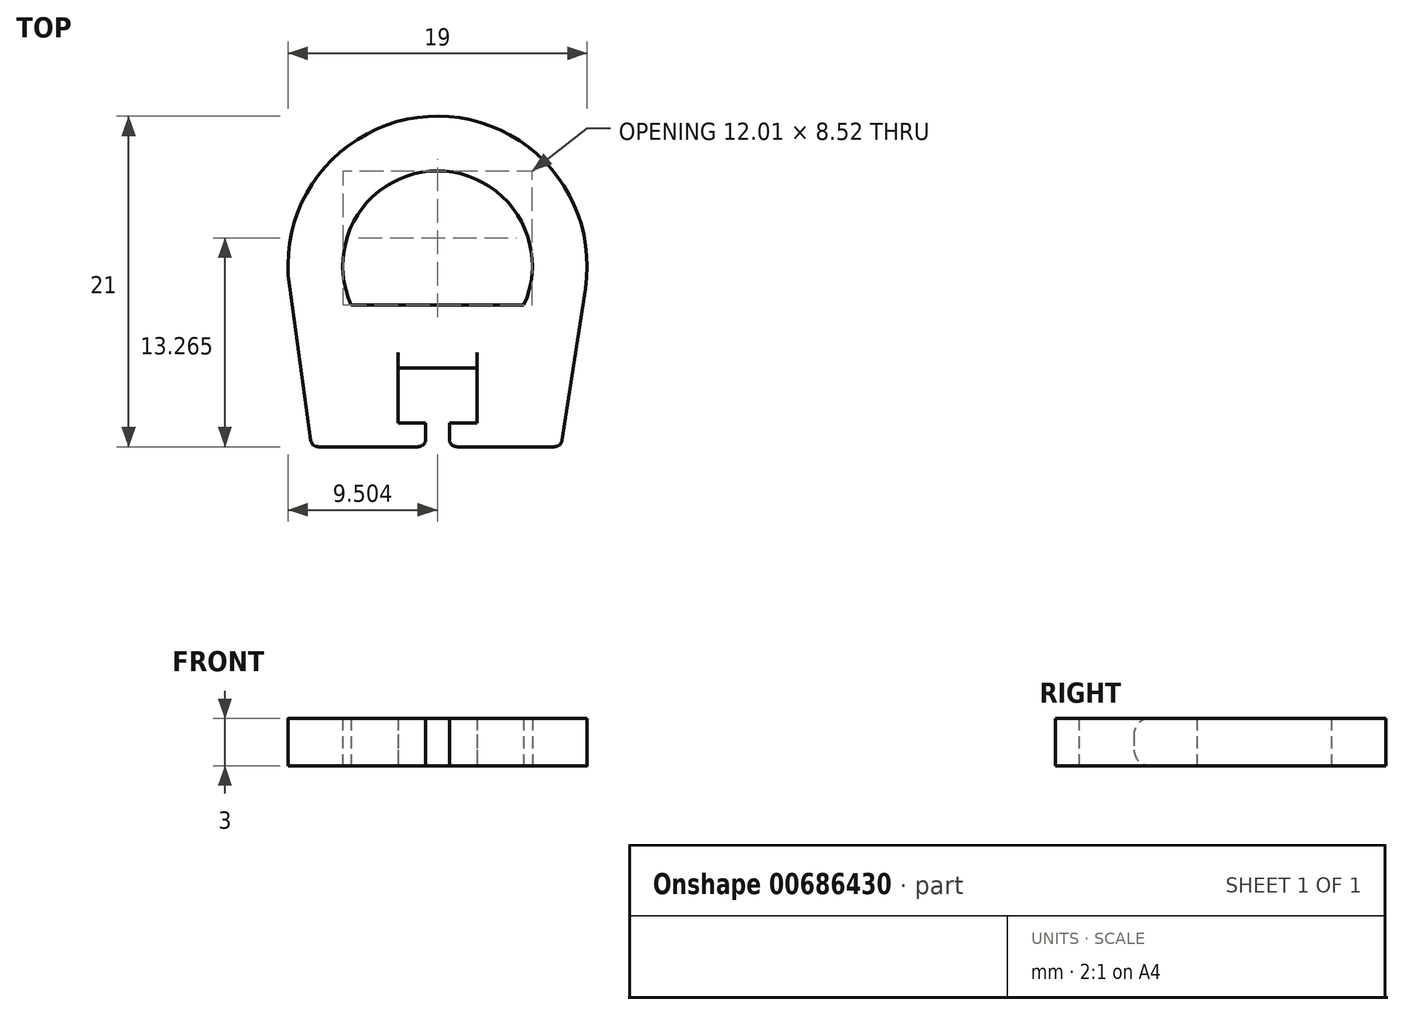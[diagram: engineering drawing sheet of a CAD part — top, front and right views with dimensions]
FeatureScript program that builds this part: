
annotation { "Feature Type Name" : "Feature", "Feature Type Description" : "" }
export const myFeature = defineFeature(function(context is Context, id is Id, definition is map)
    precondition{}
    {
        {
            var Q0;
            Q0=qCreatedBy(makeId("Top.planeOp"),FACE);
            var sketch = newSketch(context, id + "F0", { "sketchPlane" : qUnion([Q0])});
            skLineSegment(sketch, "E0.bottom", {"start": v(-28.7, 14.07) * mm, "end": v(-23.7, 14.07) * mm});
            skLineSegment(sketch, "E0.left", {"start": v(-28.7, 14.07) * mm, "end": v(-28.7, 10.57) * mm});
            skLineSegment(sketch, "E0.right", {"start": v(-23.7, 14.07) * mm, "end": v(-23.7, 10.57) * mm});
            skArc(sketch, "E1", {"start": v(-16.82, 19.13) * mm, "mid": v(-26.13, 30.07) * mm, "end": v(-35.62, 19.27) * mm});
            skPoint(sketch, "E1.centerSnap0", {"position": v(-26.2, 14.07) * mm});
            skLineSegment(sketch, "E2.0", {"start": v(-29.8, 9.07) * mm, "end": v(-26.96, 9.07) * mm});
            skLineSegment(sketch, "E3.0", {"start": v(-28.7, 10.57) * mm, "end": v(-26.96, 10.57) * mm});
            skLineSegment(sketch, "E4.0", {"start": v(-25.46, 10.57) * mm, "end": v(-25.46, 9.57) * mm});
            skLineSegment(sketch, "E5.0", {"start": v(-26.96, 10.57) * mm, "end": v(-26.96, 9.57) * mm});
            skPoint(sketch, "E6.end.orphan", {"position": v(-26.2, 9.07) * mm});
            skPoint(sketch, "E6.start.orphan", {"position": v(-26.2, 10.57) * mm});
            skLineSegment(sketch, "E7.trimOffspring", {"start": v(-25.46, 9.07) * mm, "end": v(-22.62, 9.07) * mm});
            skLineSegment(sketch, "E8.trimOffspring", {"start": v(-25.46, 9.07) * mm, "end": v(-23.7, 9.07) * mm});
            skLineSegment(sketch, "E9.trimOffspring", {"start": v(-25.46, 10.57) * mm, "end": v(-23.7, 10.57) * mm});
            skLineSegment(sketch, "E10", {"start": v(-33.77, 9.07) * mm, "end": v(-27.46, 9.07) * mm});
            skLineSegment(sketch, "E11.trimOffspring", {"start": v(-24.96, 9.07) * mm, "end": v(-18.8, 9.07) * mm});
            skLineSegment(sketch, "E12", {"start": v(-18.3, 9.5) * mm, "end": v(-16.82, 19.13) * mm});
            skLineSegment(sketch, "E13", {"start": v(-34.27, 9.5) * mm, "end": v(-35.62, 19.27) * mm});
            skLineSegment(sketch, "E14.0", {"start": v(-31.68, 18.07) * mm, "end": v(-20.73, 18.07) * mm});
            skArc(sketch, "E15.trimOffspring", {"start": v(-20.73, 18.07) * mm, "mid": v(-26.2, 26.6) * mm, "end": v(-31.68, 18.07) * mm});
            skPoint(sketch, "E16.visualSharp", {"position": v(-25.46, 9.07) * mm});
            skArc(sketch, "E16.filletArc", {"start": v(-25.46, 9.57) * mm, "mid": v(-25.31, 9.22) * mm, "end": v(-24.96, 9.07) * mm});
            skPoint(sketch, "E17.visualSharp", {"position": v(-26.96, 9.07) * mm});
            skArc(sketch, "E17.filletArc", {"start": v(-27.46, 9.07) * mm, "mid": v(-27.1, 9.22) * mm, "end": v(-26.96, 9.57) * mm});
            skPoint(sketch, "E18.visualSharp", {"position": v(-18.36, 9.07) * mm});
            skArc(sketch, "E18.filletArc", {"start": v(-18.8, 9.07) * mm, "mid": v(-18.47, 9.2) * mm, "end": v(-18.3, 9.5) * mm});
            skPoint(sketch, "E19.visualSharp", {"position": v(-34.2, 9.07) * mm});
            skArc(sketch, "E19.filletArc", {"start": v(-34.27, 9.5) * mm, "mid": v(-34.1, 9.2) * mm, "end": v(-33.77, 9.07) * mm});
            skSolve(sketch);
        }
        {
            var Q0;
            Q0=makeQuery(id+"F0.imprint","IMPRINT",FACE,{"disambiguationData":[TD([[makeQuery(id+"F0.imprint","IMPRINT",EDGE,{"derivedFrom":sQuery(id+"F0.wireOp",EDGE,"E0.bottom")}),1.0]])]});
            extrude(context, id + "F1", {"entities" : qUnion([Q0]), "depth" : 3 * mm, "offsetDistance" : 25 * mm});
        }
        {
            var Q0;
            Q0=makeQuery(id+"F1.opExtrude","CAP_EDGE",EDGE,{"disambiguationData":[OSD([sQuery(id+"F0.wireOp",EDGE,"E0.bottom")])],"isStart":false});
            var Q1;
            Q1=makeQuery(id+"F1.opExtrude","CAP_EDGE",EDGE,{"disambiguationData":[OSD([sQuery(id+"F0.wireOp",EDGE,"E0.bottom")])],"isStart":true});
            fillet(context, id + "F2", {"entities" : qUnion([Q0, Q1]), "radius" : 1 * mm, "tangentPropagation" : true, "allowEdgeOverflow" : false});
        }
    });
